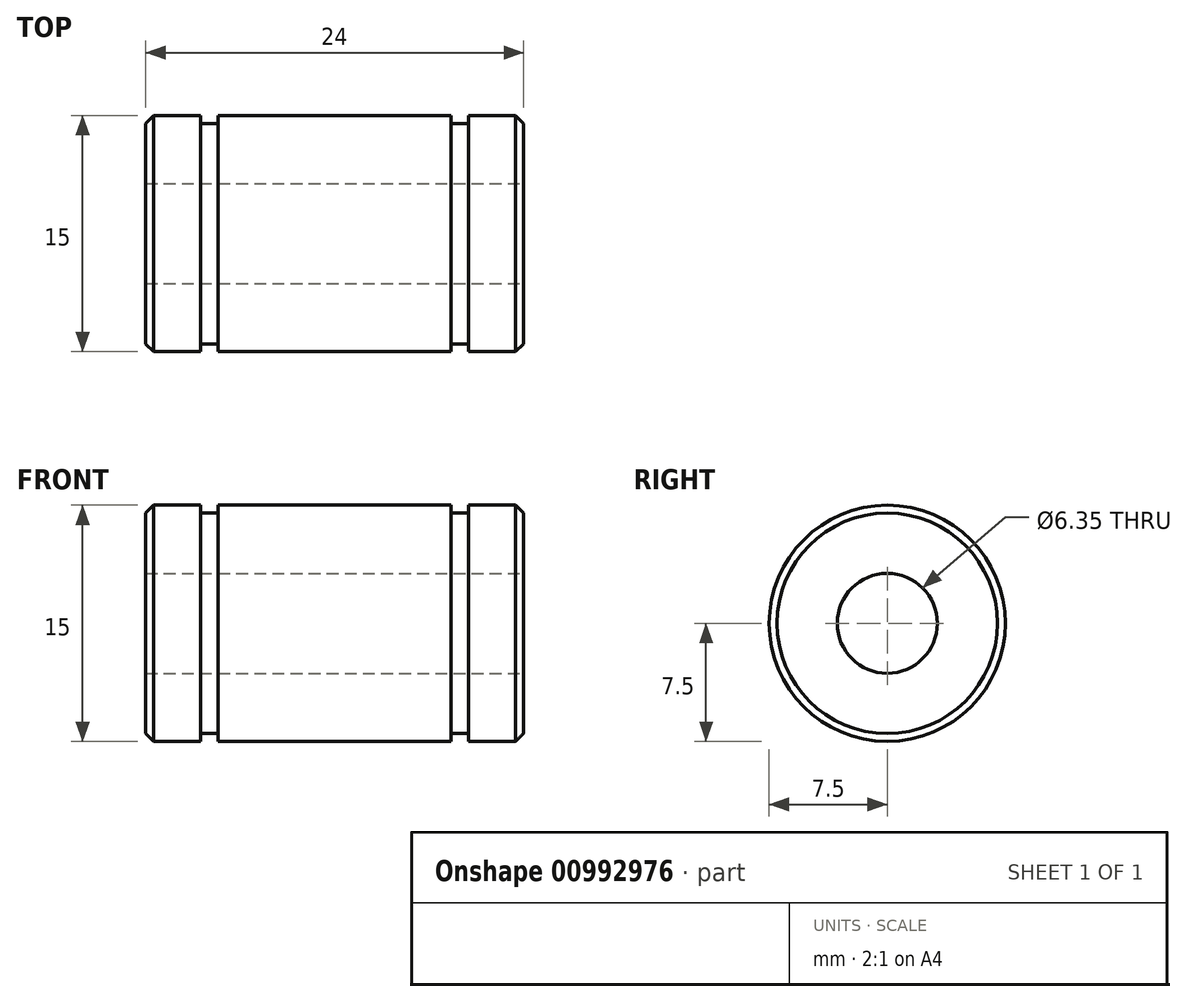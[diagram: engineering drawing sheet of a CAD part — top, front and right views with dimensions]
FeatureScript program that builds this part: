
annotation { "Feature Type Name" : "Feature", "Feature Type Description" : "" }
export const myFeature = defineFeature(function(context is Context, id is Id, definition is map)
    precondition{}
    {
        {
            var Q0;
            Q0=qCreatedBy(makeId("Right.planeOp"),FACE);
            var sketch = newSketch(context, id + "F0", { "sketchPlane" : qUnion([Q0])});
            skCircle(sketch, "E0", {"center": v(0, 0) * mm, "radius": 7.5 * mm});
            skSolve(sketch);
        }
        {
            var Q0;
            Q0 = qSketchRegion(id + "F0", true);
            extrude(context, id + "F1", {"entities" : qUnion([Q0]), "endBound" : BoundingType.SYMMETRIC, "depth" : 24 * mm, "offsetDistance" : 25.4 * mm});
        }
        {
            var Q0;
            Q0=makeQuery(id+"F1.opExtrude","CAP_FACE",FACE,{"disambiguationData":[OSD([sQuery(id+"F0.wireOp",EDGE,"E0")])],"isStart":false});
            var sketch = newSketch(context, id + "F2", { "sketchPlane" : qUnion([Q0])});
            skCircle(sketch, "E1", {"center": v(0, 0) * mm, "radius": 4 * mm});
            skSolve(sketch);
        }
        {
            var Q0;
            Q0=sQuery(id+"F2.wireOp",VERTEX,"E1.center");
            var Q1;
            Q1=makeQuery(id+"F1.opExtrude","SWEPT_BODY",BODY,{"disambiguationData":[OSD([sQuery(id+"F0.wireOp",EDGE,"E0")])]});
            hole(context, id + "F3", {"style" : HoleStyle.SIMPLE, "endStyle" : HoleEndStyle.THROUGH, "holeDiameter" : 6.35 * mm, "majorDiameter" : 6.35 * mm, "isTappedThrough" : true, "tappedDepth" : 12.7 * mm, "tapClearance" : 3, "locations" : qUnion([Q0]), "scope" : qUnion([Q1])});
        }
        {
            var Q0;
            Q0=makeQuery(id+"F1.opExtrude","CAP_EDGE",EDGE,{"disambiguationData":[OSD([sQuery(id+"F0.wireOp",EDGE,"E0")])],"isStart":false});
            var Q1;
            Q1=makeQuery(id+"F1.opExtrude","CAP_EDGE",EDGE,{"disambiguationData":[OSD([sQuery(id+"F0.wireOp",EDGE,"E0")])],"isStart":true});
            var Q2;
            Q2=makeQuery(id+"F3.hole-0.boolean.opBoolean","INTERSECT",EDGE,{"derivedFrom":[makeQuery(id+"F1.opExtrude","CAP_FACE",FACE,{"disambiguationData":[OSD([sQuery(id+"F0.wireOp",EDGE,"E0")])],"isStart":true}),makeQuery(id+"F3.hole-0.opRevolve","SWEPT_FACE",FACE,{"disambiguationData":[OSD([sQuery(id+"F3.hole-0.sketch.wireOp",EDGE,"core_line_2")])]})]});
            chamfer(context, id + "F4", {"entities" : qUnion([Q0, Q1, Q2]), "width" : 0.5 * mm, "tangentPropagation" : true});
        }
        {
            var Q0;
            Q0=qCreatedBy(makeId("Front.planeOp"),FACE);
            var sketch = newSketch(context, id + "F5", { "sketchPlane" : qUnion([Q0])});
            skLineSegment(sketch, "E2.bottom", {"start": v(-8.5, 10.98) * mm, "end": v(-7.4, 10.98) * mm});
            skLineSegment(sketch, "E2.top", {"start": v(-8.5, 7) * mm, "end": v(-7.4, 7) * mm});
            skLineSegment(sketch, "E2.left", {"start": v(-8.5, 10.98) * mm, "end": v(-8.5, 7) * mm});
            skLineSegment(sketch, "E2.right", {"start": v(-7.4, 10.98) * mm, "end": v(-7.4, 7) * mm});
            skLineSegment(sketch, "E3", {"start": v(-13.13, 0) * mm, "end": v(12.04, 0) * mm});
            skLineSegment(sketch, "E4.bottom", {"start": v(7.4, 10.98) * mm, "end": v(8.5, 10.98) * mm});
            skLineSegment(sketch, "E4.top", {"start": v(7.4, 7) * mm, "end": v(8.5, 7) * mm});
            skLineSegment(sketch, "E4.left", {"start": v(7.4, 10.98) * mm, "end": v(7.4, 7) * mm});
            skLineSegment(sketch, "E4.right", {"start": v(8.5, 10.98) * mm, "end": v(8.5, 7) * mm});
            skSolve(sketch);
        }
        {
            var Q0;
            Q0=makeQuery(id+"F5.imprint","IMPRINT",FACE,{"disambiguationData":[TD([[makeQuery(id+"F5.imprint","IMPRINT",EDGE,{"derivedFrom":sQuery(id+"F5.wireOp",EDGE,"E2.bottom")}),-1.0]])]});
            var Q1;
            Q1=makeQuery(id+"F5.imprint","IMPRINT",FACE,{"disambiguationData":[TD([[makeQuery(id+"F5.imprint","IMPRINT",EDGE,{"derivedFrom":sQuery(id+"F5.wireOp",EDGE,"E4.bottom")}),-1.0]])]});
            var Q2;
            Q2=sQuery(id+"F5.wireOp",EDGE,"E3");
            revolve(context, id + "F6", {"operationType" : NewBodyOperationType.REMOVE, "surfaceOperationType" : NewSurfaceOperationType.NEW, "entities" : qUnion([Q0, Q1]), "axis" : qUnion([Q2]), "revolveType" : RevolveType.FULL});
        }
    });
